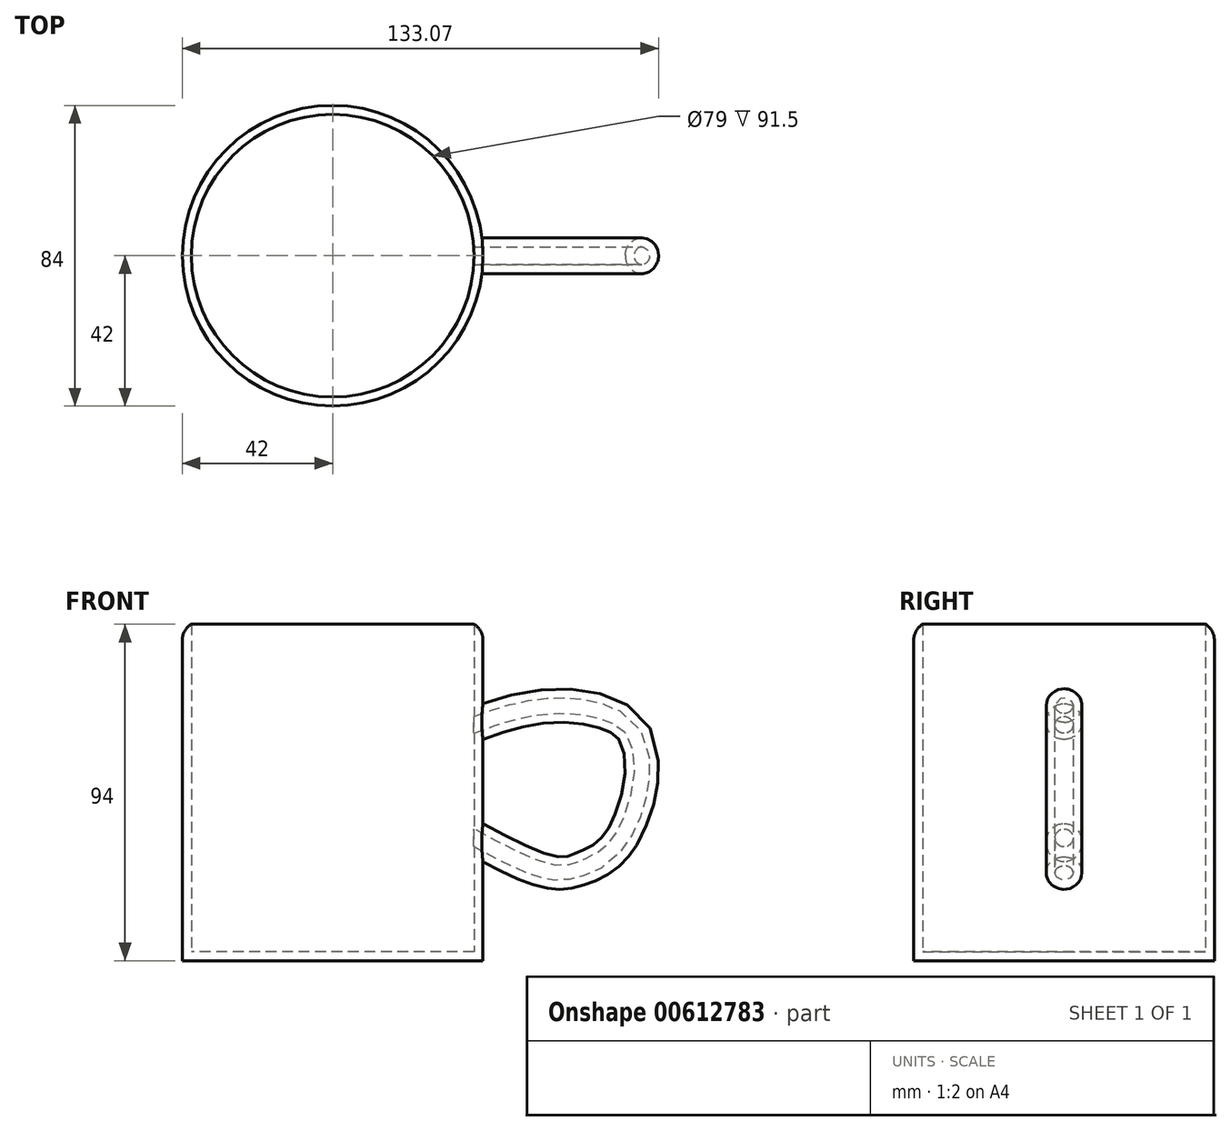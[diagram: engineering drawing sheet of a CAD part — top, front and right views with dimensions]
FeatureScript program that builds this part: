
annotation { "Feature Type Name" : "Feature", "Feature Type Description" : "" }
export const myFeature = defineFeature(function(context is Context, id is Id, definition is map)
    precondition{}
    {
        {
            var Q0;
            Q0=qCreatedBy(makeId("Top.planeOp"),FACE);
            var sketch = newSketch(context, id + "F0", { "sketchPlane" : qUnion([Q0])});
            skCircle(sketch, "E0", {"center": v(0, 0) * mm, "radius": 42 * mm});
            skSolve(sketch);
        }
        {
            var Q0;
            Q0 = qSketchRegion(id + "F0", true);
            extrude(context, id + "F1", {"entities" : qUnion([Q0]), "depth" : 94 * mm, "offsetDistance" : 25 * mm});
        }
        {
            var Q0;
            Q0=qCreatedBy(makeId("Front.planeOp"),FACE);
            var sketch = newSketch(context, id + "F2", { "sketchPlane" : qUnion([Q0])});
            skFitSpline(sketch, "E1", {"points": [v(30.5, 66.4) * mm, v(61.64, 75.05) * mm, v(88.03, 64.24) * mm, v(83.27, 31.36) * mm, v(69.43, 21.85) * mm, v(58.61, 21.41) * mm, v(32.23, 33.96) * mm], "startDerivative": vector(155.9, 64.15) * mm, "endDerivative": vector(-160.49, 89.4) * mm});
            skSolve(sketch);
        }
        {
            var Q0;
            Q0=qCreatedBy(makeId("Right.planeOp"),FACE);
            cPlane(context, id + "F3", {"entities" : qUnion([Q0]), "cplaneType" : CPlaneType.OFFSET, "offset" : 42 * mm, "width" : 150 * mm, "height" : 150 * mm});
        }
        {
            var Q0;
            Q0=qCreatedBy(id+"F3.planeOp",FACE);
            var sketch = newSketch(context, id + "F4", { "sketchPlane" : qUnion([Q0])});
            skCircle(sketch, "E2", {"center": v(0, 66.83) * mm, "radius": 5 * mm});
            skSolve(sketch);
        }
        {
            var Q0;
            Q0=makeQuery(id+"F4.imprint","IMPRINT",FACE,{"disambiguationData":[TD([[makeQuery(id+"F4.imprint","IMPRINT",EDGE,{"derivedFrom":sQuery(id+"F4.wireOp",EDGE,"E2")}),1.0]])]});
            var Q1;
            Q1=sQuery(id+"F2.wireOp",EDGE,"E1");
            sweep(context, id + "F5", {"operationType" : NewBodyOperationType.ADD, "profiles" : qUnion([Q0]), "path" : qUnion([Q1])});
        }
        {
            var Q0;
            Q0=makeQuery(id+"F1.opExtrude","CAP_FACE",FACE,{"disambiguationData":[OSD([sQuery(id+"F0.wireOp",EDGE,"E0")])],"isStart":false});
            shell(context, id + "F6", {"entities" : qUnion([Q0]), "thickness" : 2.5 * mm});
        }
        {
            var Q0;
            Q0=makeQuery(id+"F1.opExtrude","CAP_EDGE",EDGE,{"disambiguationData":[OSD([sQuery(id+"F0.wireOp",EDGE,"E0")])],"isStart":false});
            fillet(context, id + "F7", {"entities" : qUnion([Q0]), "radius" : 5 * mm, "tangentPropagation" : true, "allowEdgeOverflow" : false});
        }
    });
